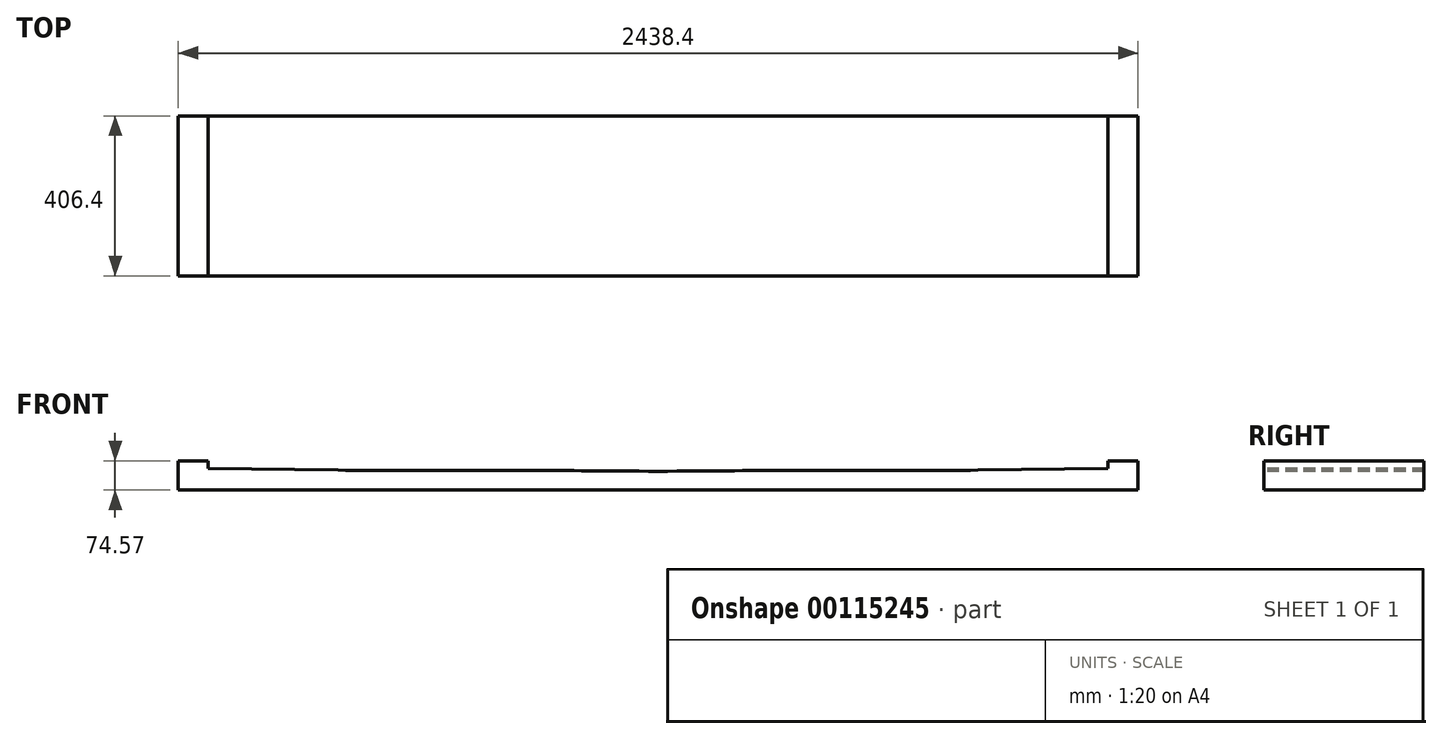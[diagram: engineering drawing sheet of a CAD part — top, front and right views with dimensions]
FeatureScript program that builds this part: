
annotation { "Feature Type Name" : "Feature", "Feature Type Description" : "" }
export const myFeature = defineFeature(function(context is Context, id is Id, definition is map)
    precondition{}
    {
        {
            var Q0;
            Q0=qCreatedBy(makeId("Front.planeOp"),FACE);
            var sketch = newSketch(context, id + "F0", { "sketchPlane" : qUnion([Q0])});
            skLineSegment(sketch, "E0", {"start": v(0, 0) * mm, "end": v(2438.4, 0) * mm});
            skLineSegment(sketch, "E1", {"start": v(1219.2, 0) * mm, "end": v(1219.2, 47.92) * mm, "construction": true});
            skArc(sketch, "E2", {"start": v(1219.2, 47.92) * mm, "mid": v(1122.08, 48.23) * mm, "end": v(1024.97, 49.16) * mm});
            skLineSegment(sketch, "E3", {"start": v(711.2, 0) * mm, "end": v(711.2, 49.92) * mm, "construction": true});
            skArc(sketch, "E4", {"start": v(1024.97, 49.16) * mm, "mid": v(868.09, 50.35) * mm, "end": v(711.2, 49.92) * mm});
            skLineSegment(sketch, "E5", {"start": v(830.74, 0) * mm, "end": v(830.74, 50.4) * mm, "construction": true});
            skLineSegment(sketch, "E6", {"start": v(1024.97, 49.16) * mm, "end": v(1024.97, 0) * mm, "construction": true});
            skArc(sketch, "E7", {"start": v(711.2, 49.92) * mm, "mid": v(558.8, 49.5) * mm, "end": v(406.4, 50.58) * mm});
            skLineSegment(sketch, "E8", {"start": v(0, 0) * mm, "end": v(0, 55.52) * mm});
            skLineSegment(sketch, "E9", {"start": v(406.4, 0) * mm, "end": v(406.4, 50.58) * mm, "construction": true});
            skLineSegment(sketch, "E10", {"start": v(406.4, 50.58) * mm, "end": v(76.2, 54.6) * mm});
            skLineSegment(sketch, "E11.0", {"start": v(76.2, 73.65) * mm, "end": v(0, 74.57) * mm});
            skLineSegment(sketch, "E12", {"start": v(76.2, 54.6) * mm, "end": v(76.2, 73.65) * mm});
            skLineSegment(sketch, "E13", {"start": v(0, 55.52) * mm, "end": v(0, 74.57) * mm});
            skArc(sketch, "E14.MirrorCS", {"start": v(1219.2, 47.92) * mm, "mid": v(1316.32, 48.23) * mm, "end": v(1413.43, 49.16) * mm});
            skArc(sketch, "E15.MirrorCS", {"start": v(1413.43, 49.16) * mm, "mid": v(1570.31, 50.35) * mm, "end": v(1727.2, 49.92) * mm});
            skArc(sketch, "E16.MirrorCS", {"start": v(1727.2, 49.92) * mm, "mid": v(1879.6, 49.5) * mm, "end": v(2032, 50.58) * mm});
            skLineSegment(sketch, "E17.MirrorCS", {"start": v(2362.2, 54.6) * mm, "end": v(2362.2, 73.65) * mm});
            skLineSegment(sketch, "E18.MirrorCS", {"start": v(2032, 50.58) * mm, "end": v(2362.2, 54.6) * mm});
            skLineSegment(sketch, "E19.MirrorCS", {"start": v(2362.2, 73.65) * mm, "end": v(2438.4, 74.57) * mm});
            skLineSegment(sketch, "E20.MirrorCS", {"start": v(2438.4, 55.52) * mm, "end": v(2438.4, 74.57) * mm});
            skLineSegment(sketch, "E21.MirrorCS", {"start": v(2438.4, 0) * mm, "end": v(2438.4, 55.52) * mm});
            skPoint(sketch, "E22.orphan", {"position": v(2438.4, 55.52) * mm});
            skLineSegment(sketch, "E23", {"start": v(1024.97, 49.16) * mm, "end": v(1219.2, 15287.92) * mm, "construction": true});
            skLineSegment(sketch, "E24", {"start": v(1219.2, 15287.92) * mm, "end": v(1219.2, 47.92) * mm, "construction": true});
            skLineSegment(sketch, "E25", {"start": v(711.2, 49.92) * mm, "end": v(830.74, -15189.6) * mm, "construction": true});
            skLineSegment(sketch, "E26", {"start": v(830.74, -15189.6) * mm, "end": v(1024.97, 49.16) * mm, "construction": true});
            skSolve(sketch);
        }
        {
            var Q0;
            Q0=makeQuery(id+"F0.imprint","IMPRINT",FACE,{"disambiguationData":[TD([[makeQuery(id+"F0.imprint","IMPRINT",EDGE,{"derivedFrom":sQuery(id+"F0.wireOp",EDGE,"E0")}),1.0]])]});
            extrude(context, id + "F1", {"entities" : qUnion([Q0]), "oppositeDirection" : true, "depth" : 406.4 * mm, "offsetDistance" : 25 * mm});
        }
    });
